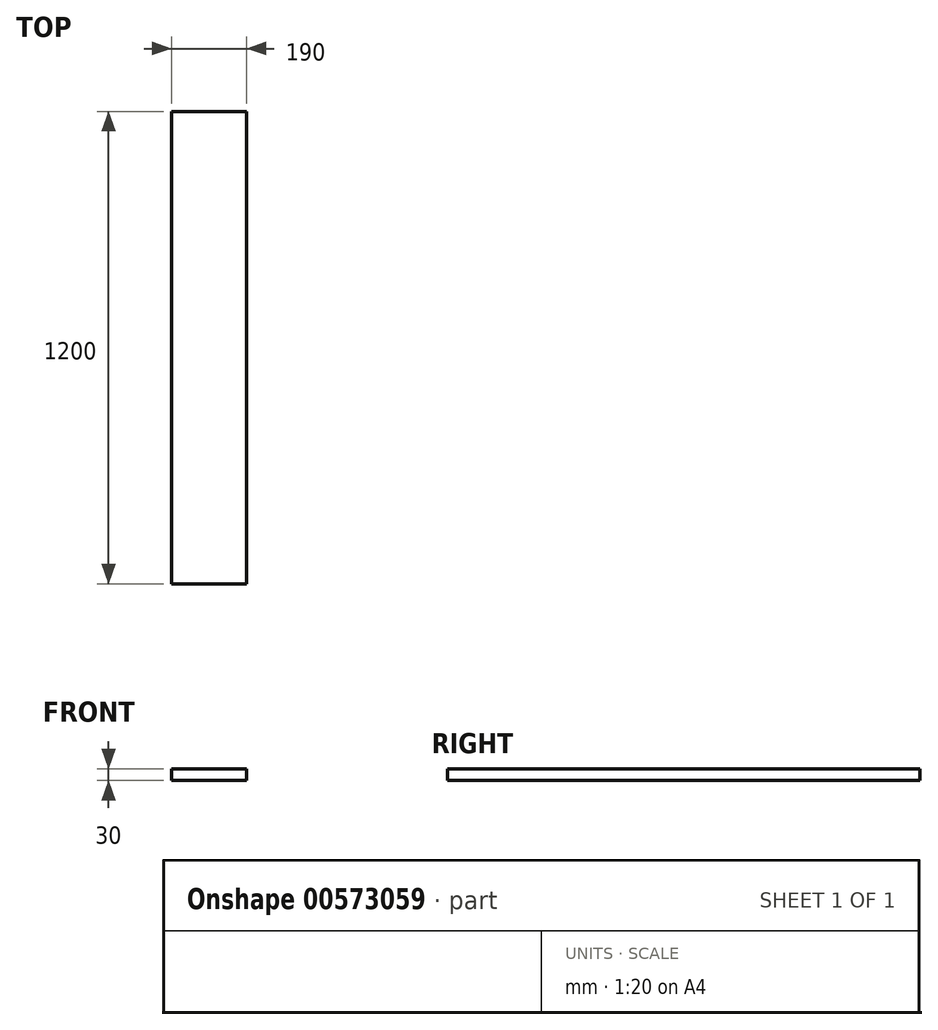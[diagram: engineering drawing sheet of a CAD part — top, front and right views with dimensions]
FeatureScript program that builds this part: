
annotation { "Feature Type Name" : "Feature", "Feature Type Description" : "" }
export const myFeature = defineFeature(function(context is Context, id is Id, definition is map)
    precondition{}
    {
        {
            var Q0;
            Q0=qCreatedBy(makeId("Front.planeOp"),FACE);
            var sketch = newSketch(context, id + "F0", { "sketchPlane" : qUnion([Q0])});
            skLineSegment(sketch, "E0.bottom", {"start": v(-81.35, 11.73) * mm, "end": v(108.65, 11.73) * mm});
            skLineSegment(sketch, "E0.top", {"start": v(-81.35, -18.27) * mm, "end": v(108.65, -18.27) * mm});
            skLineSegment(sketch, "E0.left", {"start": v(-81.35, 11.73) * mm, "end": v(-81.35, -18.27) * mm});
            skLineSegment(sketch, "E0.right", {"start": v(108.65, 11.73) * mm, "end": v(108.65, -18.27) * mm});
            skSolve(sketch);
        }
        {
            var Q0;
            Q0 = qSketchRegion(id + "F0", true);
            extrude(context, id + "F1", {"entities" : qUnion([Q0]), "depth" : 1200 * mm, "offsetDistance" : 25 * mm});
        }
    });
